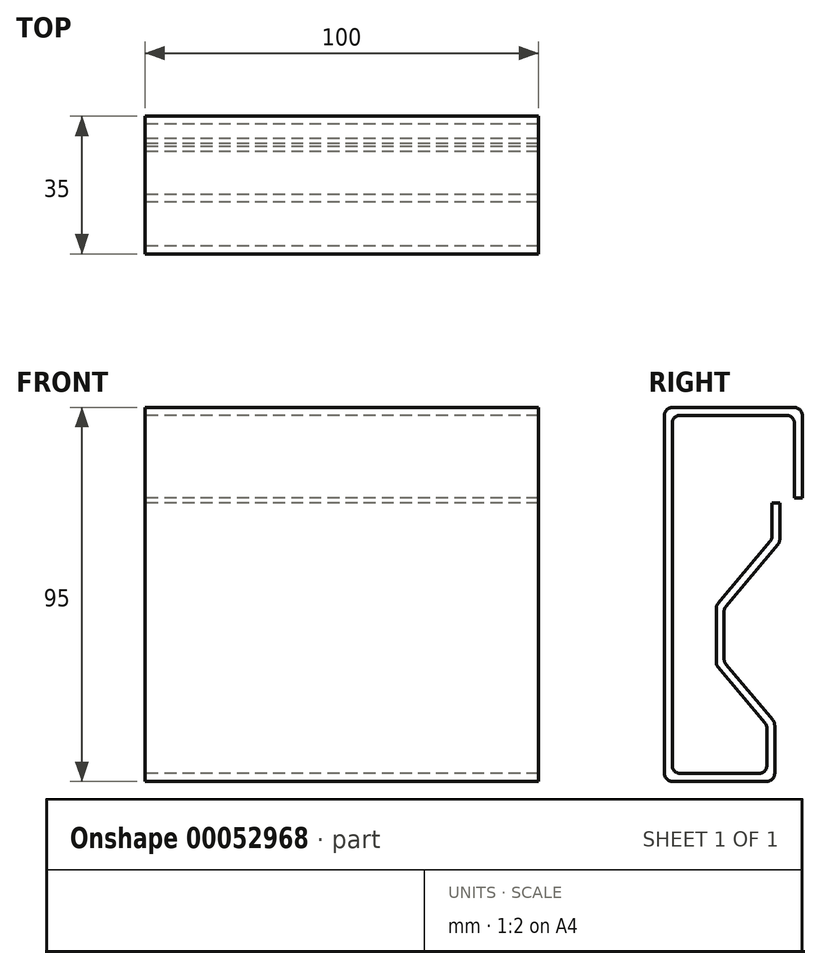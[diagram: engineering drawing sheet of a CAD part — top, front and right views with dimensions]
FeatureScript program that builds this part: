
annotation { "Feature Type Name" : "Feature", "Feature Type Description" : "" }
export const myFeature = defineFeature(function(context is Context, id is Id, definition is map)
    precondition{}
    {
        {
            var Q0;
            Q0=qCreatedBy(makeId("Right.planeOp"),FACE);
            var sketch = newSketch(context, id + "F0", { "sketchPlane" : qUnion([Q0])});
            skLineSegment(sketch, "E0", {"start": v(35, -23) * mm, "end": v(35, 0) * mm});
            skLineSegment(sketch, "E1", {"start": v(35, 0) * mm, "end": v(0, 0) * mm});
            skLineSegment(sketch, "E2", {"start": v(0, 0) * mm, "end": v(0, -95) * mm});
            skLineSegment(sketch, "E3", {"start": v(0, -95) * mm, "end": v(28, -95) * mm});
            skLineSegment(sketch, "E4", {"start": v(33, -23) * mm, "end": v(35, -23) * mm});
            skLineSegment(sketch, "E5.1", {"start": v(2, -2) * mm, "end": v(2, -93) * mm});
            skLineSegment(sketch, "E5.2", {"start": v(33, -2) * mm, "end": v(2, -2) * mm});
            skLineSegment(sketch, "E5.3", {"start": v(33, -23) * mm, "end": v(33, -2) * mm});
            skLineSegment(sketch, "E6", {"start": v(28, -95) * mm, "end": v(28, -80) * mm});
            skLineSegment(sketch, "E7", {"start": v(28, -80) * mm, "end": v(15.14, -64.68) * mm});
            skLineSegment(sketch, "E8", {"start": v(15.14, -51.13) * mm, "end": v(29.29, -34.28) * mm});
            skLineSegment(sketch, "E9", {"start": v(29.29, -34.28) * mm, "end": v(29.29, -24.28) * mm});
            skLineSegment(sketch, "E10.0", {"start": v(27.29, -33.55) * mm, "end": v(27.29, -24.28) * mm});
            skLineSegment(sketch, "E10.1", {"start": v(2, -93) * mm, "end": v(26, -93) * mm});
            skLineSegment(sketch, "E10.2", {"start": v(26, -93) * mm, "end": v(26, -80.73) * mm});
            skLineSegment(sketch, "E10.3", {"start": v(26, -80.73) * mm, "end": v(13.14, -65.4) * mm});
            skLineSegment(sketch, "E10.4", {"start": v(13.14, -50.4) * mm, "end": v(27.29, -33.55) * mm});
            skLineSegment(sketch, "E11", {"start": v(29.29, -24.28) * mm, "end": v(27.29, -24.28) * mm});
            skLineSegment(sketch, "E12", {"start": v(13.14, -65.4) * mm, "end": v(13.14, -50.4) * mm});
            skLineSegment(sketch, "E13", {"start": v(15.14, -64.68) * mm, "end": v(15.14, -51.13) * mm});
            skSolve(sketch);
        }
        {
            var Q0;
            Q0=makeQuery(id+"F0.imprint","IMPRINT",FACE,{"disambiguationData":[TD([[makeQuery(id+"F0.imprint","IMPRINT",EDGE,{"derivedFrom":sQuery(id+"F0.wireOp",EDGE,"E0")}),1.0]])]});
            extrude(context, id + "F1", {"entities" : qUnion([Q0]), "depth" : 100 * mm});
        }
        {
            var Q0;
            Q0=makeQuery(id+"F1.opExtrude","SWEPT_EDGE",EDGE,{"disambiguationData":[OSD([sQuery(id+"F0.wireOp",EDGE,"E0"),sQuery(id+"F0.wireOp",EDGE,"E1")])]});
            var Q1;
            Q1=makeQuery(id+"F1.opExtrude","SWEPT_EDGE",EDGE,{"disambiguationData":[OSD([sQuery(id+"F0.wireOp",EDGE,"E1"),sQuery(id+"F0.wireOp",EDGE,"E2")])]});
            var Q2;
            Q2=makeQuery(id+"F1.opExtrude","SWEPT_EDGE",EDGE,{"disambiguationData":[OSD([sQuery(id+"F0.wireOp",EDGE,"E5.2"),sQuery(id+"F0.wireOp",EDGE,"E5.3")])]});
            var Q3;
            Q3=makeQuery(id+"F1.opExtrude","SWEPT_EDGE",EDGE,{"disambiguationData":[OSD([sQuery(id+"F0.wireOp",EDGE,"E5.1"),sQuery(id+"F0.wireOp",EDGE,"E5.2")])]});
            var Q4;
            Q4=makeQuery(id+"F1.opExtrude","SWEPT_EDGE",EDGE,{"disambiguationData":[OSD([sQuery(id+"F0.wireOp",EDGE,"E2"),sQuery(id+"F0.wireOp",EDGE,"E3")])]});
            var Q5;
            Q5=makeQuery(id+"F1.opExtrude","SWEPT_EDGE",EDGE,{"disambiguationData":[OSD([sQuery(id+"F0.wireOp",EDGE,"E3"),sQuery(id+"F0.wireOp",EDGE,"E6")])]});
            var Q6;
            Q6=makeQuery(id+"F1.opExtrude","SWEPT_EDGE",EDGE,{"disambiguationData":[OSD([sQuery(id+"F0.wireOp",EDGE,"E6"),sQuery(id+"F0.wireOp",EDGE,"E7")])]});
            var Q7;
            Q7=makeQuery(id+"F1.opExtrude","SWEPT_EDGE",EDGE,{"disambiguationData":[OSD([sQuery(id+"F0.wireOp",EDGE,"E7"),sQuery(id+"F0.wireOp",EDGE,"E8")])]});
            var Q8;
            Q8=makeQuery(id+"F1.opExtrude","SWEPT_EDGE",EDGE,{"disambiguationData":[OSD([sQuery(id+"F0.wireOp",EDGE,"E8"),sQuery(id+"F0.wireOp",EDGE,"E9")])]});
            var Q9;
            Q9=makeQuery(id+"F1.opExtrude","SWEPT_EDGE",EDGE,{"disambiguationData":[OSD([sQuery(id+"F0.wireOp",EDGE,"E5.1"),sQuery(id+"F0.wireOp",EDGE,"E10.1")])]});
            var Q10;
            Q10=makeQuery(id+"F1.opExtrude","SWEPT_EDGE",EDGE,{"disambiguationData":[OSD([sQuery(id+"F0.wireOp",EDGE,"E10.1"),sQuery(id+"F0.wireOp",EDGE,"E10.2")])]});
            var Q11;
            Q11=makeQuery(id+"F1.opExtrude","SWEPT_EDGE",EDGE,{"disambiguationData":[OSD([sQuery(id+"F0.wireOp",EDGE,"E10.2"),sQuery(id+"F0.wireOp",EDGE,"E10.3")])]});
            var Q12;
            Q12=makeQuery(id+"F1.opExtrude","SWEPT_EDGE",EDGE,{"disambiguationData":[OSD([sQuery(id+"F0.wireOp",EDGE,"E10.3"),sQuery(id+"F0.wireOp",EDGE,"E10.4")])]});
            var Q13;
            Q13=makeQuery(id+"F1.opExtrude","SWEPT_EDGE",EDGE,{"disambiguationData":[OSD([sQuery(id+"F0.wireOp",EDGE,"E10.0"),sQuery(id+"F0.wireOp",EDGE,"E10.4")])]});
            fillet(context, id + "F2", {"entities" : qUnion([Q0, Q1, Q2, Q3, Q4, Q5, Q6, Q7, Q8, Q9, Q10, Q11, Q12, Q13]), "radius" : 2 * mm, "tangentPropagation" : true, "allowEdgeOverflow" : false});
        }
    });
